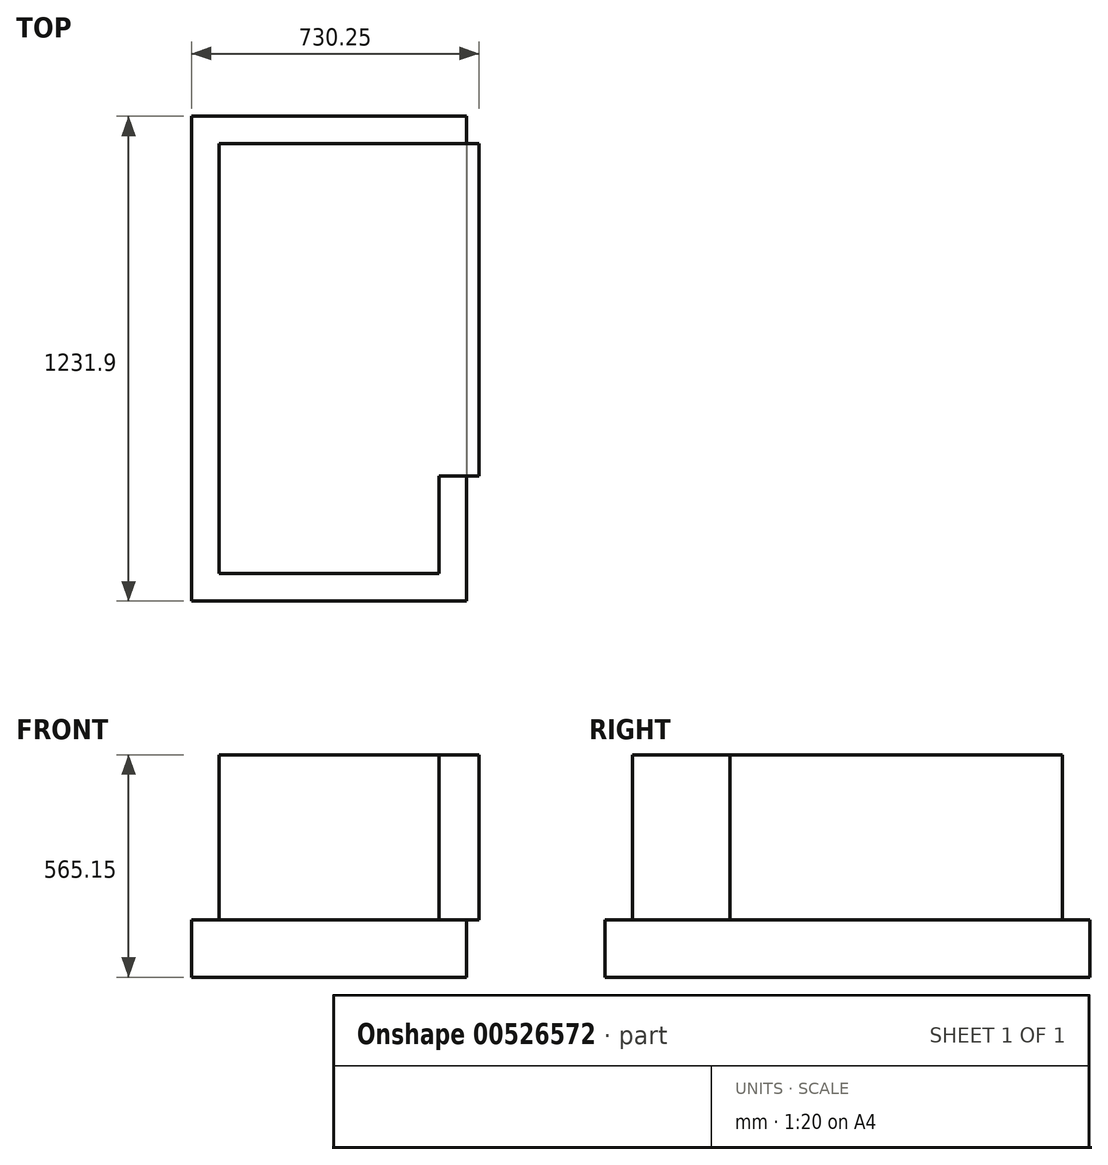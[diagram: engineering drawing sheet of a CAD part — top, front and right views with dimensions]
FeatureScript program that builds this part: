
annotation { "Feature Type Name" : "Feature", "Feature Type Description" : "" }
export const myFeature = defineFeature(function(context is Context, id is Id, definition is map)
    precondition{}
    {
        {
            var Q0;
            Q0=qCreatedBy(makeId("Top.planeOp"),FACE);
            var sketch = newSketch(context, id + "F0", { "sketchPlane" : qUnion([Q0])});
            skLineSegment(sketch, "E0.bottom", {"start": v(0, 0) * mm, "end": v(558.8, 0) * mm});
            skLineSegment(sketch, "E0.top", {"start": v(0, 1092.2) * mm, "end": v(558.8, 1092.2) * mm});
            skLineSegment(sketch, "E0.left", {"start": v(0, 0) * mm, "end": v(0, 1092.2) * mm});
            skLineSegment(sketch, "E0.right", {"start": v(558.8, 0) * mm, "end": v(558.8, 247.65) * mm});
            skLineSegment(sketch, "E1", {"start": v(558.8, 1092.2) * mm, "end": v(660.4, 1092.2) * mm});
            skLineSegment(sketch, "E2", {"start": v(660.4, 1092.2) * mm, "end": v(660.4, 247.65) * mm});
            skLineSegment(sketch, "E3", {"start": v(660.4, 247.65) * mm, "end": v(558.8, 247.65) * mm});
            skLineSegment(sketch, "E4", {"start": v(558.8, 247.65) * mm, "end": v(558.8, 1092.2) * mm, "construction": true});
            skSolve(sketch);
        }
        {
            var Q0;
            Q0 = qSketchRegion(id + "F0", true);
            extrude(context, id + "F1", {"entities" : qUnion([Q0]), "depth" : 419.1 * mm, "offsetDistance" : 25.4 * mm});
        }
        {
            var Q0;
            Q0=qCreatedBy(makeId("Top.planeOp"),FACE);
            var sketch = newSketch(context, id + "F2", { "sketchPlane" : qUnion([Q0])});
            skLineSegment(sketch, "E5.bottom", {"start": v(-69.85, 1162.05) * mm, "end": v(628.65, 1162.05) * mm});
            skLineSegment(sketch, "E5.top", {"start": v(-69.85, -69.85) * mm, "end": v(628.65, -69.85) * mm});
            skLineSegment(sketch, "E5.left", {"start": v(-69.85, 1162.05) * mm, "end": v(-69.85, -69.85) * mm});
            skLineSegment(sketch, "E5.right", {"start": v(628.65, 1162.05) * mm, "end": v(628.65, 958.85) * mm});
            skLineSegment(sketch, "E6", {"start": v(628.65, 133.35) * mm, "end": v(679.45, 133.35) * mm, "construction": true});
            skLineSegment(sketch, "E7", {"start": v(679.45, 133.35) * mm, "end": v(679.45, 958.85) * mm, "construction": true});
            skLineSegment(sketch, "E8", {"start": v(679.45, 958.85) * mm, "end": v(628.65, 958.85) * mm, "construction": true});
            skLineSegment(sketch, "E9", {"start": v(628.65, 958.85) * mm, "end": v(628.65, 133.35) * mm});
            skLineSegment(sketch, "E10", {"start": v(628.65, 133.35) * mm, "end": v(628.65, -69.85) * mm});
            skLineSegment(sketch, "E11", {"start": v(0, 0) * mm, "end": v(-69.85, 0) * mm, "construction": true});
            skLineSegment(sketch, "E12", {"start": v(628.65, 0) * mm, "end": v(558.8, 0) * mm, "construction": true});
            skLineSegment(sketch, "E13", {"start": v(0, 0) * mm, "end": v(0, -69.85) * mm, "construction": true});
            skLineSegment(sketch, "E14", {"start": v(0, 1162.05) * mm, "end": v(0, 1092.2) * mm, "construction": true});
            skSolve(sketch);
        }
        {
            var Q0;
            Q0 = qSketchRegion(id + "F2", true);
            extrude(context, id + "F3", {"entities" : qUnion([Q0]), "operationType" : NewBodyOperationType.ADD, "oppositeDirection" : true, "depth" : 146.05 * mm, "offsetDistance" : 25.4 * mm});
        }
    });
